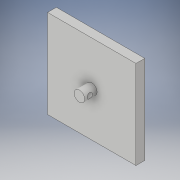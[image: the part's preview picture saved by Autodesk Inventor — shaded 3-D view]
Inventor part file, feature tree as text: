
AUTODESK INVENTOR PART (.ipt)
format: ipt  version: 2019 (Build 230136000, 136)  size: 112,640 bytes
history: native  units: mm
features: sketch x3, extrude x2, plane x1, hole x1
ambient origin geometry x8: Origin, YZ Plane, XZ Plane, XY Plane, X Axis, Y Axis, Z Axis, Center Point
bodies: Solid1 (feature_tree)
feature tree (7):
  extrude  "Extrusion1"  Depth=50.0mm
  extrude  "Extrusion2"  Depth=25.0mm
  plane  "Work Plane1"
  hole  "Hole1"  [1 undecoded]
  sketch  "Sketch1"  dims[d0=50.0mm d1=50.0mm]
  sketch  "Sketch2"  dims[d2=25.0mm d3=25.0mm]
  sketch  "Sketch3"  dims[d4=5.0mm d5=0.0mm d6=6.0mm d7=7.0mm d8=0.0mm d9=4.0mm d10=3.0mm d11=6.0mm d12=4.0mm d13=2.0mm d14=90.0deg d15=8.0mm d16=20.594885mm]
note: 1 required parameter value undecoded (feature->parameter linkage not recoverable at this tier; creation-order binding heuristic only, values carry confidence <= 0.55)
